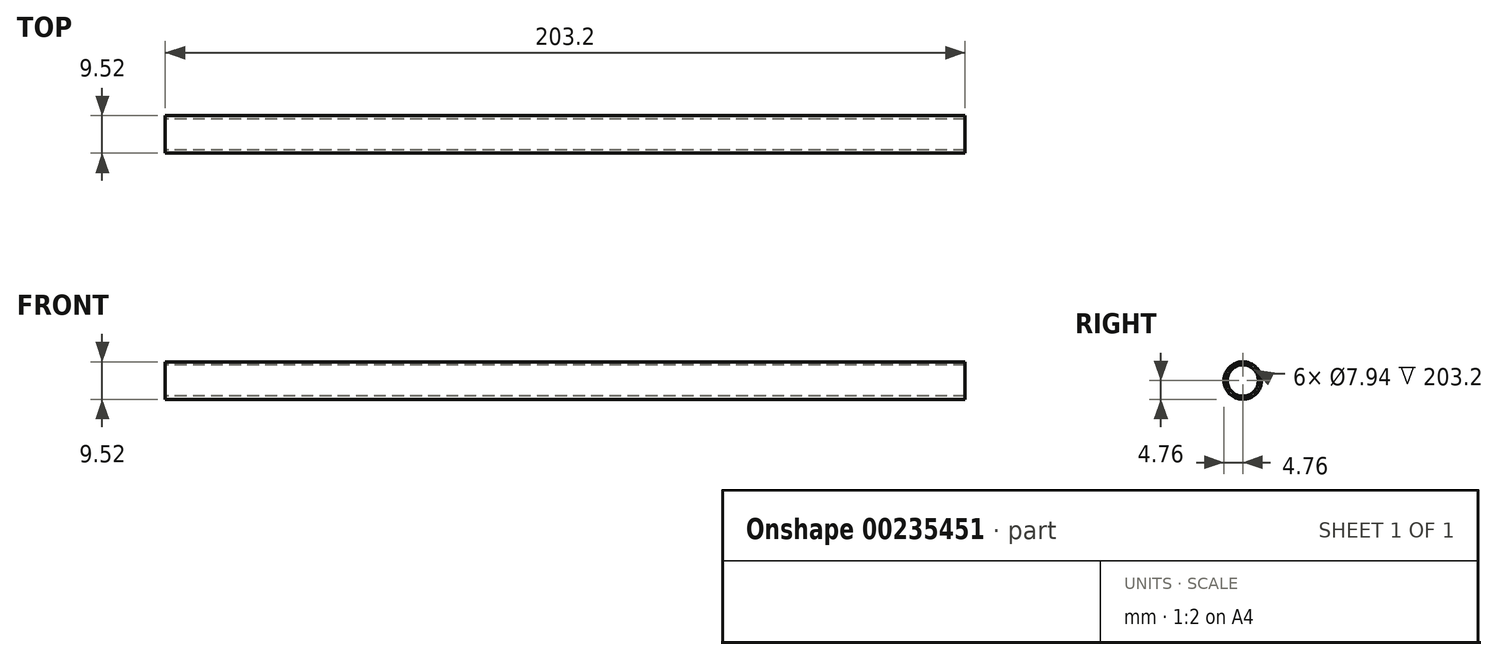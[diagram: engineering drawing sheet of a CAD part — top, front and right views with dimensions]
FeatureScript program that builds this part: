
annotation { "Feature Type Name" : "Feature", "Feature Type Description" : "" }
export const myFeature = defineFeature(function(context is Context, id is Id, definition is map)
    precondition{}
    {
        {
            var Q0;
            Q0=qCreatedBy(makeId("Right.planeOp"),FACE);
            var sketch = newSketch(context, id + "F0", { "sketchPlane" : qUnion([Q0])});
            skCircle(sketch, "E0", {"center": v(0, 0) * mm, "radius": 4.76 * mm});
            skCircle(sketch, "E1", {"center": v(0, 0) * mm, "radius": 3.97 * mm});
            skSolve(sketch);
        }
        {
            var Q0;
            Q0 = qSketchRegion(id + "F0", true);
            extrude(context, id + "F1", {"entities" : qUnion([Q0]), "depth" : 203.2 * mm});
        }
    });
